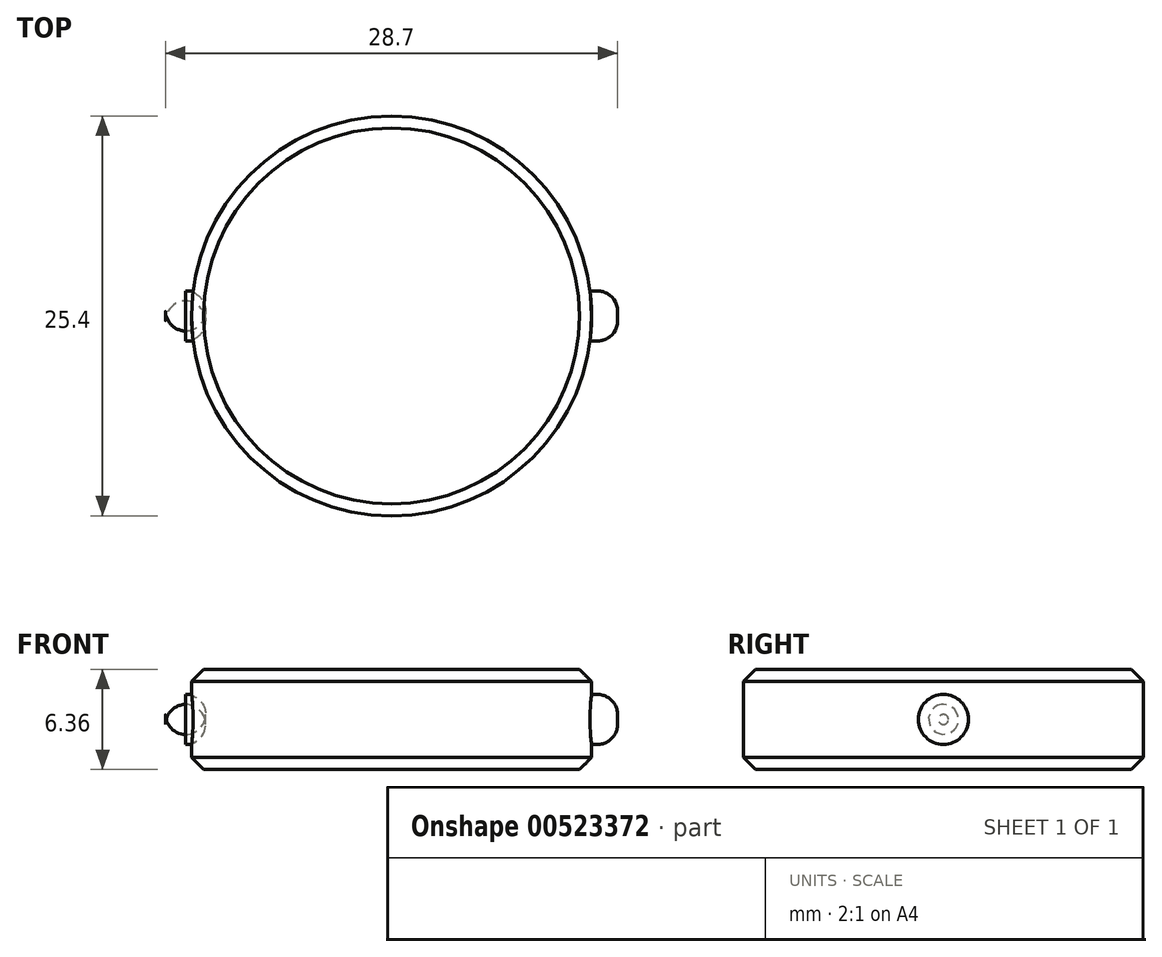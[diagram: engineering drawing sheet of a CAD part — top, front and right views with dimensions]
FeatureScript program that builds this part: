
annotation { "Feature Type Name" : "Feature", "Feature Type Description" : "" }
export const myFeature = defineFeature(function(context is Context, id is Id, definition is map)
    precondition{}
    {
        {
            var Q0;
            Q0=qCreatedBy(makeId("Top.planeOp"),FACE);
            var sketch = newSketch(context, id + "F0", { "sketchPlane" : qUnion([Q0])});
            skCircle(sketch, "E0", {"center": v(0, 0) * mm, "radius": 12.7 * mm});
            skSolve(sketch);
        }
        {
            var Q0;
            Q0=makeQuery(id+"F0.imprint","IMPRINT",FACE,{"disambiguationData":[TD([[makeQuery(id+"F0.imprint","IMPRINT",EDGE,{"derivedFrom":sQuery(id+"F0.wireOp",EDGE,"E0")}),1.0]])]});
            extrude(context, id + "F1", {"entities" : qUnion([Q0]), "endBound" : BoundingType.SYMMETRIC, "depth" : 6.35 * mm, "offsetDistance" : 25.4 * mm});
        }
        {
            var Q0;
            Q0=qCreatedBy(makeId("Right.planeOp"),FACE);
            var sketch = newSketch(context, id + "F2", { "sketchPlane" : qUnion([Q0])});
            skCircle(sketch, "E1", {"center": v(0, 0) * mm, "radius": 1.59 * mm});
            skSolve(sketch);
        }
        {
            var Q0;
            Q0 = qSketchRegion(id + "F2", true);
            extrude(context, id + "F3", {"entities" : qUnion([Q0]), "operationType" : NewBodyOperationType.ADD, "oppositeDirection" : true, "depth" : 14.35 * mm, "offsetDistance" : 25.4 * mm, "hasSecondDirection" : true, "secondDirectionOppositeDirection" : false, "secondDirectionDepth" : 14.35 * mm});
        }
        {
            var Q0;
            Q0=makeQuery(id+"F3.opExtrude","CAP_EDGE",EDGE,{"disambiguationData":[OSD([sQuery(id+"F2.wireOp",EDGE,"E1")])],"isStart":false});
            var Q1;
            Q1=makeQuery(id+"F3.opExtrude","CAP_EDGE",EDGE,{"disambiguationData":[OSD([sQuery(id+"F2.wireOp",EDGE,"E1")])],"isStart":true});
            fillet(context, id + "F4", {"entities" : qUnion([Q0, Q1]), "radius" : 1.27 * mm, "allowEdgeOverflow" : false});
        }
        {
            var Q0;
            Q0=makeQuery(id+"F1.opExtrude","CAP_EDGE",EDGE,{"disambiguationData":[OSD([sQuery(id+"F0.wireOp",EDGE,"E0")])],"isStart":false});
            var Q1;
            Q1=makeQuery(id+"F1.opExtrude","CAP_EDGE",EDGE,{"disambiguationData":[OSD([sQuery(id+"F0.wireOp",EDGE,"E0")])],"isStart":true});
            chamfer(context, id + "F5", {"entities" : qUnion([Q0, Q1]), "width" : 0.76 * mm, "tangentPropagation" : true});
        }
    });
